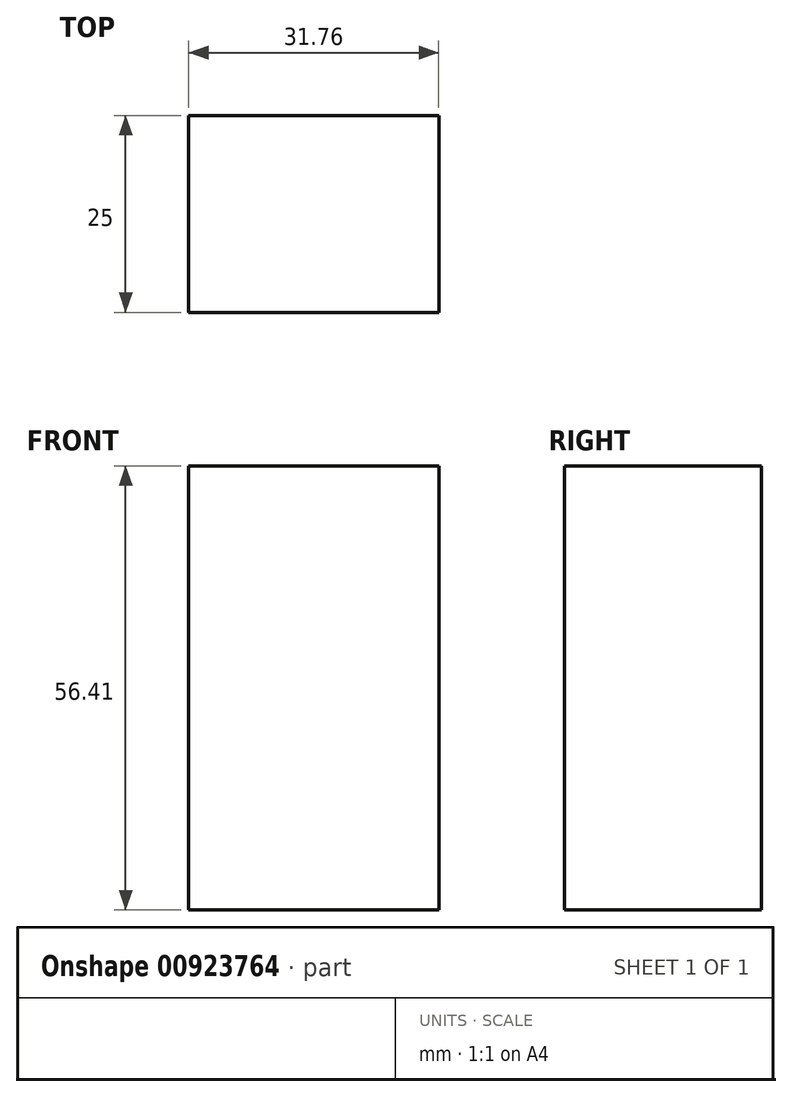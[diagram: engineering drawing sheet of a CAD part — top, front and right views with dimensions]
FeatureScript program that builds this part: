
annotation { "Feature Type Name" : "Feature", "Feature Type Description" : "" }
export const myFeature = defineFeature(function(context is Context, id is Id, definition is map)
    precondition{}
    {
        {
            var Q0;
            Q0=qCreatedBy(makeId("Front.planeOp"),FACE);
            var sketch = newSketch(context, id + "F0", { "sketchPlane" : qUnion([Q0])});
            skLineSegment(sketch, "E0", {"start": v(-27.95, 31.33) * mm, "end": v(3.81, 31.33) * mm});
            skLineSegment(sketch, "E1", {"start": v(3.81, 31.33) * mm, "end": v(3.81, -25.08) * mm});
            skLineSegment(sketch, "E2", {"start": v(-27.95, 31.33) * mm, "end": v(-27.95, -25.08) * mm});
            skLineSegment(sketch, "E3", {"start": v(-27.95, -25.08) * mm, "end": v(3.81, -25.08) * mm});
            skSolve(sketch);
        }
        {
            var Q0;
            Q0=makeQuery(id+"F0.imprint","IMPRINT",FACE,{"disambiguationData":[TD([[makeQuery(id+"F0.imprint","IMPRINT",EDGE,{"derivedFrom":sQuery(id+"F0.wireOp",EDGE,"E0")}),-1.0]])]});
            extrude(context, id + "F1", {"entities" : qUnion([Q0]), "depth" : 25 * mm, "offsetDistance" : 25 * mm});
        }
    });
